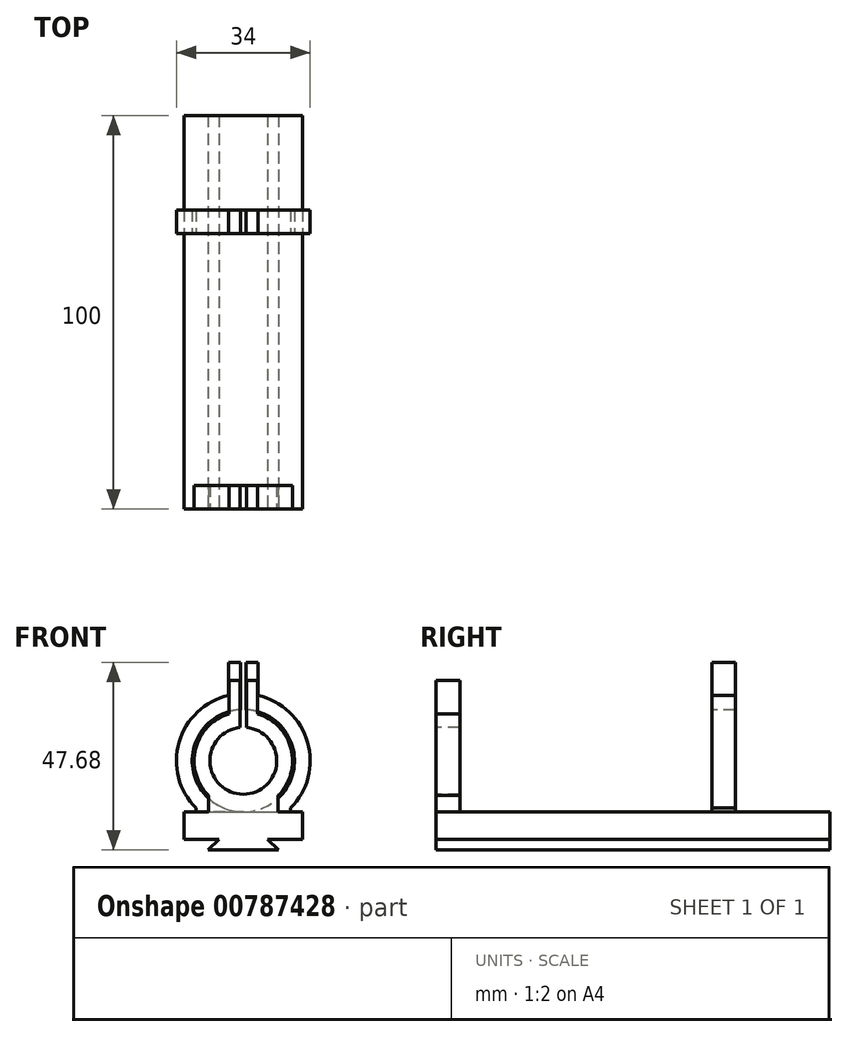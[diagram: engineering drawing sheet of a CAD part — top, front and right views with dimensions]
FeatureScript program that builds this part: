
annotation { "Feature Type Name" : "Feature", "Feature Type Description" : "" }
export const myFeature = defineFeature(function(context is Context, id is Id, definition is map)
    precondition{}
    {
        {
            var Q0;
            Q0=qCreatedBy(makeId("Front.planeOp"),FACE);
            var sketch = newSketch(context, id + "F0", { "sketchPlane" : qUnion([Q0])});
            skLineSegment(sketch, "E0", {"start": v(0, 0) * mm, "end": v(-15, 0) * mm});
            skLineSegment(sketch, "E1", {"start": v(-15, 0) * mm, "end": v(-15, 7) * mm});
            skLineSegment(sketch, "E2", {"start": v(-15, 7) * mm, "end": v(15, 7) * mm});
            skLineSegment(sketch, "E3", {"start": v(15, 7) * mm, "end": v(15, 0) * mm});
            skLineSegment(sketch, "E4", {"start": v(15, 0) * mm, "end": v(0, 0) * mm});
            skArc(sketch, "E5", {"start": v(-0.8, 28.46) * mm, "mid": v(0, 11.5) * mm, "end": v(0.8, 28.46) * mm});
            skArc(sketch, "E6", {"start": v(-3.62, 31.96) * mm, "mid": v(-12.12, 23.04) * mm, "end": v(-8.84, 11.16) * mm});
            skLineSegment(sketch, "E7", {"start": v(0.8, 28.46) * mm, "end": v(0.8, 40.46) * mm});
            skLineSegment(sketch, "E8", {"start": v(0.8, 40.46) * mm, "end": v(3.62, 40.46) * mm});
            skLineSegment(sketch, "E9", {"start": v(3.62, 40.46) * mm, "end": v(3.62, 31.96) * mm});
            skLineSegment(sketch, "E10.MirrorCS", {"start": v(-0.8, 28.46) * mm, "end": v(-0.8, 40.46) * mm});
            skLineSegment(sketch, "E11.MirrorCS", {"start": v(-0.8, 40.46) * mm, "end": v(-3.62, 40.46) * mm});
            skLineSegment(sketch, "E12.MirrorCS", {"start": v(-3.62, 40.46) * mm, "end": v(-3.62, 31.96) * mm});
            skLineSegment(sketch, "E13", {"start": v(-8.84, 11.16) * mm, "end": v(-8.84, 7) * mm});
            skLineSegment(sketch, "E14.MirrorCS", {"start": v(8.84, 11.16) * mm, "end": v(8.84, 7) * mm});
            skPoint(sketch, "E15.orphan", {"position": v(0, 7) * mm});
            skArc(sketch, "E16.trimOffspring", {"start": v(8.84, 11.16) * mm, "mid": v(12.12, 23.04) * mm, "end": v(3.62, 31.96) * mm});
            skLineSegment(sketch, "E17", {"start": v(0, 0) * mm, "end": v(0, -2.7) * mm});
            skLineSegment(sketch, "E18", {"start": v(0, -2.7) * mm, "end": v(-8.9, -2.7) * mm});
            skLineSegment(sketch, "E19", {"start": v(-8.9, -2.7) * mm, "end": v(-6.2, 0) * mm});
            skLineSegment(sketch, "E20.MirrorCS", {"start": v(0, -2.7) * mm, "end": v(8.9, -2.7) * mm});
            skLineSegment(sketch, "E21.MirrorCS", {"start": v(8.9, -2.7) * mm, "end": v(6.2, 0) * mm});
            skLineSegment(sketch, "E22", {"start": v(0, 20) * mm, "end": v(0, 7) * mm});
            skSolve(sketch);
        }
        {
            var Q0;
            Q0=qCreatedBy(makeId("Front.planeOp"),FACE);
            var sketch = newSketch(context, id + "F1", { "sketchPlane" : qUnion([Q0])});
            skLineSegment(sketch, "E23", {"start": v(0, 0) * mm, "end": v(0, 7) * mm});
            skArc(sketch, "E24", {"start": v(-0.75, 32.98) * mm, "mid": v(0, 7) * mm, "end": v(0.75, 32.98) * mm});
            skArc(sketch, "E25", {"start": v(-3.75, 36.58) * mm, "mid": v(-16.33, 24.72) * mm, "end": v(-12.02, 7.98) * mm});
            skLineSegment(sketch, "E26", {"start": v(0, 7) * mm, "end": v(-12.02, 7) * mm});
            skLineSegment(sketch, "E27", {"start": v(0, 7) * mm, "end": v(12.02, 7) * mm});
            skLineSegment(sketch, "E28", {"start": v(0.75, 32.98) * mm, "end": v(0.75, 44.98) * mm});
            skLineSegment(sketch, "E29", {"start": v(0.75, 44.98) * mm, "end": v(3.75, 44.98) * mm});
            skLineSegment(sketch, "E30", {"start": v(3.75, 44.98) * mm, "end": v(3.75, 36.58) * mm});
            skLineSegment(sketch, "E31.MirrorCS", {"start": v(-0.75, 32.98) * mm, "end": v(-0.75, 44.98) * mm});
            skLineSegment(sketch, "E32.MirrorCS", {"start": v(-3.75, 44.98) * mm, "end": v(-3.75, 36.58) * mm});
            skLineSegment(sketch, "E33", {"start": v(-12.02, 7.98) * mm, "end": v(-12.02, 7) * mm});
            skLineSegment(sketch, "E34", {"start": v(12.02, 7.98) * mm, "end": v(12.02, 7) * mm});
            skArc(sketch, "E35.trimOffspring", {"start": v(12.02, 7.98) * mm, "mid": v(16.33, 24.72) * mm, "end": v(3.75, 36.58) * mm});
            skLineSegment(sketch, "E36", {"start": v(0, 20) * mm, "end": v(0, 7) * mm});
            skLineSegment(sketch, "E37", {"start": v(-3.75, 44.98) * mm, "end": v(-0.75, 44.98) * mm});
            skSolve(sketch);
        }
        {
            var Q0;
            Q0=makeQuery(id+"F0.imprint","IMPRINT",FACE,{"disambiguationData":[TD([[makeQuery(id+"F0.imprint","IMPRINT",EDGE,{"derivedFrom":sQuery(id+"F0.wireOp",EDGE,"E0")}),-1.0]])]});
            var Q1;
            {var subQ0=sQuery(id+"F0.wireOp",EDGE,"E17");Q1=makeQuery(id+"F0.imprint","IMPRINT",FACE,{"disambiguationData":[TD([[makeQuery(id+"F0.imprint","IMPRINT",EDGE,{"derivedFrom":subQ0}),-1.0]])]});}
            var Q2;
            {var subQ0=sQuery(id+"F0.wireOp",EDGE,"E17");Q2=makeQuery(id+"F0.imprint","IMPRINT",FACE,{"disambiguationData":[TD([[makeQuery(id+"F0.imprint","IMPRINT",EDGE,{"derivedFrom":subQ0}),1.0]])]});}
            extrude(context, id + "F2", {"entities" : qUnion([Q0, Q1, Q2]), "oppositeDirection" : true, "depth" : 100 * mm, "offsetDistance" : 25 * mm});
        }
        {
            var Q0;
            Q0=makeQuery(id+"F1.imprint","IMPRINT",FACE,{"disambiguationData":[TD([[makeQuery(id+"F1.imprint","IMPRINT",EDGE,{"derivedFrom":sQuery(id+"F1.wireOp",EDGE,"E24")}),-1.0]])]});
            extrude(context, id + "F3", {"entities" : qUnion([Q0]), "operationType" : NewBodyOperationType.ADD, "oppositeDirection" : true, "depth" : 76 * mm, "offsetDistance" : 25 * mm});
        }
        {
            var Q0;
            Q0=makeQuery(id+"F1.imprint","IMPRINT",FACE,{"disambiguationData":[TD([[makeQuery(id+"F1.imprint","IMPRINT",EDGE,{"derivedFrom":sQuery(id+"F1.wireOp",EDGE,"E24")}),-1.0]])]});
            extrude(context, id + "F4", {"entities" : qUnion([Q0]), "operationType" : NewBodyOperationType.REMOVE, "oppositeDirection" : true, "depth" : 70 * mm, "offsetDistance" : 25 * mm});
        }
        {
            var Q0;
            Q0=makeQuery(id+"F0.imprint","IMPRINT",FACE,{"disambiguationData":[TD([[makeQuery(id+"F0.imprint","IMPRINT",EDGE,{"derivedFrom":sQuery(id+"F0.wireOp",EDGE,"E5")}),-1.0]])]});
            extrude(context, id + "F5", {"entities" : qUnion([Q0]), "operationType" : NewBodyOperationType.ADD, "oppositeDirection" : true, "depth" : 6 * mm, "offsetDistance" : 25 * mm});
        }
        {
            var Q0;
            Q0=qCreatedBy(makeId("Right.planeOp"),FACE);
            var sketch = newSketch(context, id + "F6", { "sketchPlane" : qUnion([Q0])});
            skLineSegment(sketch, "E38", {"start": v(0, 0) * mm, "end": v(0, 58.56) * mm});
            skLineSegment(sketch, "E39", {"start": v(0, 58.56) * mm, "end": v(3, 58.56) * mm});
            skLineSegment(sketch, "E40", {"start": v(3, 58.56) * mm, "end": v(3, 54.06) * mm});
            skCircle(sketch, "E41", {"center": v(3, 54.06) * mm, "radius": 1.5 * mm});
            skLineSegment(sketch, "E42", {"start": v(0, 0) * mm, "end": v(73, 0) * mm});
            skLineSegment(sketch, "E43", {"start": v(73, 0) * mm, "end": v(73, 63.08) * mm});
            skLineSegment(sketch, "E44", {"start": v(73, 63.08) * mm, "end": v(73, 58.58) * mm});
            skCircle(sketch, "E45", {"center": v(73, 58.58) * mm, "radius": 1.5 * mm});
            skSolve(sketch);
        }
        {
            var Q0;
            {var subQ0=sQuery(id+"F6.wireOp",EDGE,"E44");var subQ1=sQuery(id+"F6.wireOp",EDGE,"E43");var subQ2=makeQuery(id+"F6.imprint","INTERSECT",VERTEX,{"derivedFrom":[subQ1,subQ0]});Q0=makeQuery(id+"F6.imprint","IMPRINT",FACE,{"disambiguationData":[TD([[makeQuery(id+"F6.imprint","IMPRINT",EDGE,{"disambiguationData":[TD([[subQ2,1.0]])],"derivedFrom":subQ1}),1.0]])]});}
            var Q1;
            {var subQ0=sQuery(id+"F6.wireOp",EDGE,"E44");var subQ1=sQuery(id+"F6.wireOp",EDGE,"E43");var subQ2=makeQuery(id+"F6.imprint","INTERSECT",VERTEX,{"derivedFrom":[subQ1,subQ0]});Q1=makeQuery(id+"F6.imprint","IMPRINT",FACE,{"disambiguationData":[TD([[makeQuery(id+"F6.imprint","IMPRINT",EDGE,{"disambiguationData":[TD([[subQ2,1.0]])],"derivedFrom":subQ1}),-1.0]])]});}
            var Q2;
            Q2=makeQuery(id+"F6.imprint","IMPRINT",FACE,{"disambiguationData":[TD([[makeQuery(id+"F6.imprint","IMPRINT",EDGE,{"derivedFrom":sQuery(id+"F6.wireOp",EDGE,"E41")}),1.0]])]});
            var Q3;
            Q3=sQuery(id+"F6.wireOp",EDGE,"E41");
            var Q4;
            Q4=sQuery(id+"F6.wireOp",EDGE,"E45");
            extrude(context, id + "F7", {"entities" : qUnion([Q0, Q1, Q2]), "operationType" : NewBodyOperationType.REMOVE, "surfaceEntities" : qUnion([Q3, Q4]), "endBound" : BoundingType.SYMMETRIC, "oppositeDirection" : true, "depth" : 25 * mm, "offsetDistance" : 25 * mm});
        }
    });
